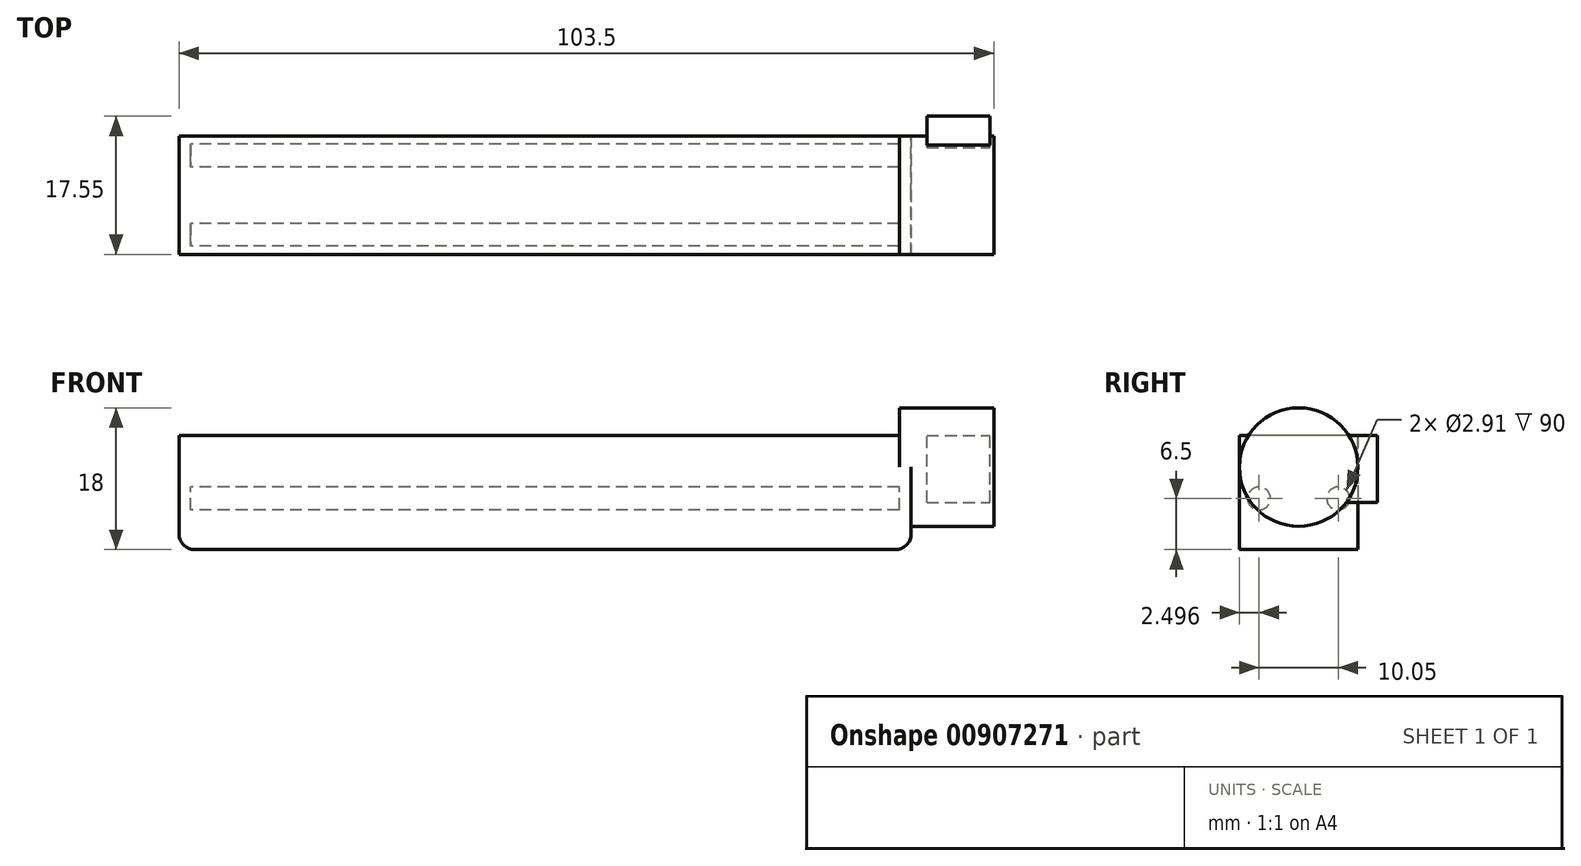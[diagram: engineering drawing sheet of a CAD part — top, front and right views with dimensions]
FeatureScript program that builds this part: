
annotation { "Feature Type Name" : "Feature", "Feature Type Description" : "" }
export const myFeature = defineFeature(function(context is Context, id is Id, definition is map)
    precondition{}
    {
        {
            var Q0;
            Q0=qCreatedBy(makeId("Top.planeOp"),FACE);
            var sketch = newSketch(context, id + "F0", { "sketchPlane" : qUnion([Q0])});
            skLineSegment(sketch, "E0.bottom", {"start": v(-46.5, -1.3) * mm, "end": v(46.5, -1.3) * mm});
            skLineSegment(sketch, "E0.top", {"start": v(-46.5, -16.34) * mm, "end": v(46.5, -16.34) * mm});
            skLineSegment(sketch, "E0.left", {"start": v(-46.5, -1.3) * mm, "end": v(-46.5, -16.34) * mm});
            skLineSegment(sketch, "E0.right", {"start": v(46.5, -1.3) * mm, "end": v(46.5, -16.34) * mm});
            skSolve(sketch);
        }
        {
            var Q0;
            Q0=qSketchRegion(id+"F0",true);
            var Q1;
            Q1=qSketchRegion(id+"F2",true);
            extrude(context, id + "F1", {"entities" : qUnion([Q0, Q1]), "depth" : 1.5 * mm, "offsetDistance" : 25 * mm});
        }
        {
            var Q0;
            Q0=makeQuery(id+"F1.opExtrude","SWEPT_FACE",FACE,{"disambiguationData":[OSD([sQuery(id+"F0.wireOp",EDGE,"E0.left")])]});
            var sketch = newSketch(context, id + "F2", { "sketchPlane" : qUnion([Q0])});
            skLineSegment(sketch, "E1.bottom", {"start": v(1.3, 0) * mm, "end": v(16.34, 0) * mm});
            skLineSegment(sketch, "E1.top", {"start": v(1.3, 14.5) * mm, "end": v(16.34, 14.5) * mm});
            skLineSegment(sketch, "E1.left", {"start": v(1.3, 0) * mm, "end": v(1.3, 14.5) * mm});
            skLineSegment(sketch, "E1.right", {"start": v(16.34, 0) * mm, "end": v(16.34, 14.5) * mm});
            skSolve(sketch);
        }
        {
            var Q0;
            {var subQ0=sQuery(id+"F2.wireOp",EDGE,"E1.top");Q0=makeQuery(id+"F2.imprint","IMPRINT",FACE,{"disambiguationData":[TD([[makeQuery(id+"F2.imprint","IMPRINT",EDGE,{"derivedFrom":subQ0}),-1.0]])]});}
            extrude(context, id + "F3", {"entities" : qUnion([Q0]), "operationType" : NewBodyOperationType.ADD, "oppositeDirection" : true, "depth" : 1.5 * mm, "offsetDistance" : 25 * mm});
        }
        {
            var Q0;
            Q0=makeQuery(id+"F1.opExtrude","CAP_EDGE",EDGE,{"disambiguationData":[OSD([sQuery(id+"F0.wireOp",EDGE,"E0.left")])],"isStart":true});
            fillet(context, id + "F4", {"entities" : qUnion([Q0]), "radius" : 2 * mm, "tangentPropagation" : true, "allowEdgeOverflow" : false});
        }
        {
            var Q0;
            Q0=makeQuery(id+"F1.opExtrude","SWEPT_FACE",FACE,{"disambiguationData":[OSD([sQuery(id+"F0.wireOp",EDGE,"E0.right")])]});
            var Q1;
            Q1=makeQuery(id+"F1.opExtrude","SWEPT_FACE",FACE,{"disambiguationData":[OSD([sQuery(id+"F0.wireOp",EDGE,"E0.right")])]});
            var sketch = newSketch(context, id + "F5", { "sketchPlane" : qUnion([Q0, Q1])});
            skLineSegment(sketch, "E2.bottom", {"start": v(-16.34, 0) * mm, "end": v(-1.3, 0) * mm});
            skLineSegment(sketch, "E2.top", {"start": v(-16.34, 10.47) * mm, "end": v(-1.3, 10.47) * mm});
            skLineSegment(sketch, "E2.left", {"start": v(-16.34, 0) * mm, "end": v(-16.34, 10.47) * mm});
            skLineSegment(sketch, "E2.right", {"start": v(-1.3, 0) * mm, "end": v(-1.3, 10.47) * mm});
            skCircle(sketch, "E3", {"center": v(-8.82, 10.47) * mm, "radius": 7.53 * mm});
            skSolve(sketch);
        }
        {
            var Q0;
            Q0=qSketchRegion(id+"F5",true);
            extrude(context, id + "F6", {"entities" : qUnion([Q0]), "operationType" : NewBodyOperationType.ADD, "oppositeDirection" : true, "depth" : 1.5 * mm, "offsetDistance" : 25 * mm});
        }
        {
            var Q0;
            Q0=makeQuery(id+"F1.opExtrude","CAP_EDGE",EDGE,{"disambiguationData":[OSD([sQuery(id+"F0.wireOp",EDGE,"E0.right")])],"isStart":true});
            fillet(context, id + "F7", {"entities" : qUnion([Q0]), "radius" : 2 * mm, "tangentPropagation" : true, "allowEdgeOverflow" : false});
        }
        {
            var Q0;
            Q0=makeQuery(id+"F6.boolean.opBoolean","MERGE",FACE,{"derivedFrom":[makeQuery(id+"F1.opExtrude","SWEPT_FACE",FACE,{"disambiguationData":[OSD([sQuery(id+"F0.wireOp",EDGE,"E0.right")])]}),makeQuery(id+"F6.opExtrude","CAP_FACE",FACE,{"disambiguationData":[OSD([sQuery(id+"F5.wireOp",EDGE,"E2.bottom"),sQuery(id+"F5.wireOp",EDGE,"E2.left"),sQuery(id+"F5.wireOp",EDGE,"E2.right"),sQuery(id+"F5.wireOp",EDGE,"E3")])],"isStart":true})]});
            var sketch = newSketch(context, id + "F8", { "sketchPlane" : qUnion([Q0])});
            skLineSegment(sketch, "E4", {"start": v(-16.34, 10.47) * mm, "end": v(-1.3, 10.47) * mm});
            skCircle(sketch, "E5", {"center": v(-8.82, 10.47) * mm, "radius": 1.5 * mm});
            skSolve(sketch);
        }
        {
            var Q0;
            Q0=qSketchRegion(id+"F8",true);
            extrude(context, id + "F9", {"entities" : qUnion([Q0]), "operationType" : NewBodyOperationType.ADD, "oppositeDirection" : true, "depth" : 93 * mm, "offsetDistance" : 25 * mm});
        }
        {
            var Q0;
            Q0=makeQuery(id+"F6.boolean.opBoolean","MERGE",FACE,{"derivedFrom":[makeQuery(id+"F1.opExtrude","SWEPT_FACE",FACE,{"disambiguationData":[OSD([sQuery(id+"F0.wireOp",EDGE,"E0.right")])]}),makeQuery(id+"F6.opExtrude","CAP_FACE",FACE,{"disambiguationData":[OSD([sQuery(id+"F5.wireOp",EDGE,"E2.bottom"),sQuery(id+"F5.wireOp",EDGE,"E2.left"),sQuery(id+"F5.wireOp",EDGE,"E2.right"),sQuery(id+"F5.wireOp",EDGE,"E3")])],"isStart":true})]});
            var sketch = newSketch(context, id + "F10", { "sketchPlane" : qUnion([Q0])});
            skLineSegment(sketch, "E6", {"start": v(-16.34, 10.47) * mm, "end": v(-1.3, 10.47) * mm});
            skCircle(sketch, "E7", {"center": v(-8.82, 10.47) * mm, "radius": 7.53 * mm});
            skSolve(sketch);
        }
        {
            var Q0;
            Q0=qSketchRegion(id+"F10",true);
            extrude(context, id + "F11", {"entities" : qUnion([Q0]), "operationType" : NewBodyOperationType.ADD, "depth" : 10.5 * mm, "offsetDistance" : 25 * mm});
        }
        {
            var Q0;
            Q0=makeQuery(id+"F3.opExtrude","CAP_FACE",FACE,{"disambiguationData":[OSD([sQuery(id+"F0.wireOp",EDGE,"E0.left"),sQuery(id+"F2.wireOp",EDGE,"E1.top"),sQuery(id+"F2.wireOp",EDGE,"E1.left"),sQuery(id+"F2.wireOp",EDGE,"E1.right")])],"isStart":false});
            var sketch = newSketch(context, id + "F12", { "sketchPlane" : qUnion([Q0])});
            skLineSegment(sketch, "E8.bottom", {"start": v(-16.34, 1.5) * mm, "end": v(-1.3, 1.5) * mm});
            skLineSegment(sketch, "E8.top", {"start": v(-16.34, 6.5) * mm, "end": v(-1.3, 6.5) * mm});
            skLineSegment(sketch, "E8.left", {"start": v(-16.34, 1.5) * mm, "end": v(-16.34, 6.5) * mm});
            skLineSegment(sketch, "E8.right", {"start": v(-1.3, 1.5) * mm, "end": v(-1.3, 6.5) * mm});
            skLineSegment(sketch, "E9", {"start": v(-16.34, 6.5) * mm, "end": v(-13.84, 6.5) * mm});
            skLineSegment(sketch, "E10", {"start": v(-1.3, 6.5) * mm, "end": v(-3.8, 6.5) * mm});
            skCircle(sketch, "E11", {"center": v(-13.84, 6.5) * mm, "radius": 1.46 * mm});
            skCircle(sketch, "E12", {"center": v(-3.8, 6.5) * mm, "radius": 1.46 * mm});
            skSolve(sketch);
        }
        {
            var Q0;
            {var subQ0=sQuery(id+"F12.wireOp",EDGE,"E9");var subQ1=sQuery(id+"F12.wireOp",EDGE,"E8.top");var subQ2=makeQuery(id+"F12.imprint","INTERSECT",VERTEX,{"derivedFrom":[subQ1,subQ0]});Q0=makeQuery(id+"F12.imprint","IMPRINT",FACE,{"disambiguationData":[TD([[makeQuery(id+"F12.imprint","IMPRINT",EDGE,{"disambiguationData":[TD([[subQ2,-1.0]])],"derivedFrom":subQ1}),1.0]])]});}
            var Q1;
            {var subQ0=sQuery(id+"F12.wireOp",EDGE,"E9");var subQ1=sQuery(id+"F12.wireOp",EDGE,"E8.top");var subQ2=makeQuery(id+"F12.imprint","INTERSECT",VERTEX,{"derivedFrom":[subQ1,subQ0]});Q1=makeQuery(id+"F12.imprint","IMPRINT",FACE,{"disambiguationData":[TD([[makeQuery(id+"F12.imprint","IMPRINT",EDGE,{"disambiguationData":[TD([[subQ2,-1.0]])],"derivedFrom":subQ1}),-1.0]])]});}
            var Q2;
            {var subQ0=sQuery(id+"F12.wireOp",EDGE,"E10");var subQ1=sQuery(id+"F12.wireOp",EDGE,"E8.top");var subQ2=makeQuery(id+"F12.imprint","INTERSECT",VERTEX,{"derivedFrom":[subQ1,subQ0]});Q2=makeQuery(id+"F12.imprint","IMPRINT",FACE,{"disambiguationData":[TD([[makeQuery(id+"F12.imprint","IMPRINT",EDGE,{"disambiguationData":[TD([[subQ2,1.0]])],"derivedFrom":subQ1}),-1.0]])]});}
            var Q3;
            {var subQ0=sQuery(id+"F12.wireOp",EDGE,"E10");var subQ1=sQuery(id+"F12.wireOp",EDGE,"E8.top");var subQ2=makeQuery(id+"F12.imprint","INTERSECT",VERTEX,{"derivedFrom":[subQ1,subQ0]});Q3=makeQuery(id+"F12.imprint","IMPRINT",FACE,{"disambiguationData":[TD([[makeQuery(id+"F12.imprint","IMPRINT",EDGE,{"disambiguationData":[TD([[subQ2,1.0]])],"derivedFrom":subQ1}),1.0]])]});}
            var Q4;
            Q4=makeQuery(id+"F6.opExtrude","CAP_FACE",FACE,{"disambiguationData":[OSD([sQuery(id+"F5.wireOp",EDGE,"E2.bottom"),sQuery(id+"F5.wireOp",EDGE,"E2.left"),sQuery(id+"F5.wireOp",EDGE,"E2.right"),sQuery(id+"F5.wireOp",EDGE,"E3")])],"isStart":false});
            extrude(context, id + "F13", {"entities" : qUnion([Q0, Q1, Q2, Q3]), "operationType" : NewBodyOperationType.ADD, "endBound" : BoundingType.UP_TO_SURFACE, "depth" : 25 * mm, "endBoundEntityFace" : qUnion([Q4]), "offsetDistance" : 25 * mm});
        }
        {
            var Q0;
            Q0=makeQuery(id+"F6.boolean.opBoolean","MERGE",FACE,{"derivedFrom":[makeQuery(id+"F3.boolean.opBoolean","MERGE",FACE,{"derivedFrom":[makeQuery(id+"F1.opExtrude","SWEPT_FACE",FACE,{"disambiguationData":[OSD([sQuery(id+"F0.wireOp",EDGE,"E0.bottom")])]}),makeQuery(id+"F3.opExtrude","SWEPT_FACE",FACE,{"disambiguationData":[OSD([sQuery(id+"F2.wireOp",EDGE,"E1.left")])]})]}),makeQuery(id+"F6.opExtrude","SWEPT_FACE",FACE,{"disambiguationData":[OSD([sQuery(id+"F5.wireOp",EDGE,"E2.right")])]})]});
            cPlane(context, id + "F14", {"entities" : qUnion([Q0]), "cplaneType" : CPlaneType.OFFSET, "offset" : 0 * mm, "width" : 150 * mm, "height" : 150 * mm});
        }
        {
            var Q0;
            Q0=qCreatedBy(id+"F14.planeOp",FACE);
            var sketch = newSketch(context, id + "F15", { "sketchPlane" : qUnion([Q0])});
            skPoint(sketch, "E13.0", {"position": v(-45, 5.99) * mm});
            skLineSegment(sketch, "E14", {"start": v(-48.5, 5.99) * mm, "end": v(-45, 5.99) * mm});
            skLineSegment(sketch, "E15.bottom", {"start": v(-48.5, 5.99) * mm, "end": v(-56.5, 5.99) * mm});
            skLineSegment(sketch, "E15.top", {"start": v(-48.5, 14.49) * mm, "end": v(-56.5, 14.49) * mm});
            skLineSegment(sketch, "E15.left", {"start": v(-48.5, 5.99) * mm, "end": v(-48.5, 14.49) * mm});
            skLineSegment(sketch, "E15.right", {"start": v(-56.5, 5.99) * mm, "end": v(-56.5, 14.49) * mm});
            skSolve(sketch);
        }
        {
            var Q0;
            Q0=makeQuery(id+"F15.imprint","IMPRINT",FACE,{"disambiguationData":[TD([[makeQuery(id+"F15.imprint","IMPRINT",EDGE,{"derivedFrom":sQuery(id+"F15.wireOp",EDGE,"E15.bottom")}),-1.0]])]});
            extrude(context, id + "F16", {"entities" : qUnion([Q0]), "operationType" : NewBodyOperationType.ADD, "depth" : 2.5 * mm, "offsetDistance" : 25 * mm, "hasSecondDirection" : true, "secondDirectionOppositeDirection" : true, "secondDirectionDepth" : 2.5 * mm});
        }
    });
